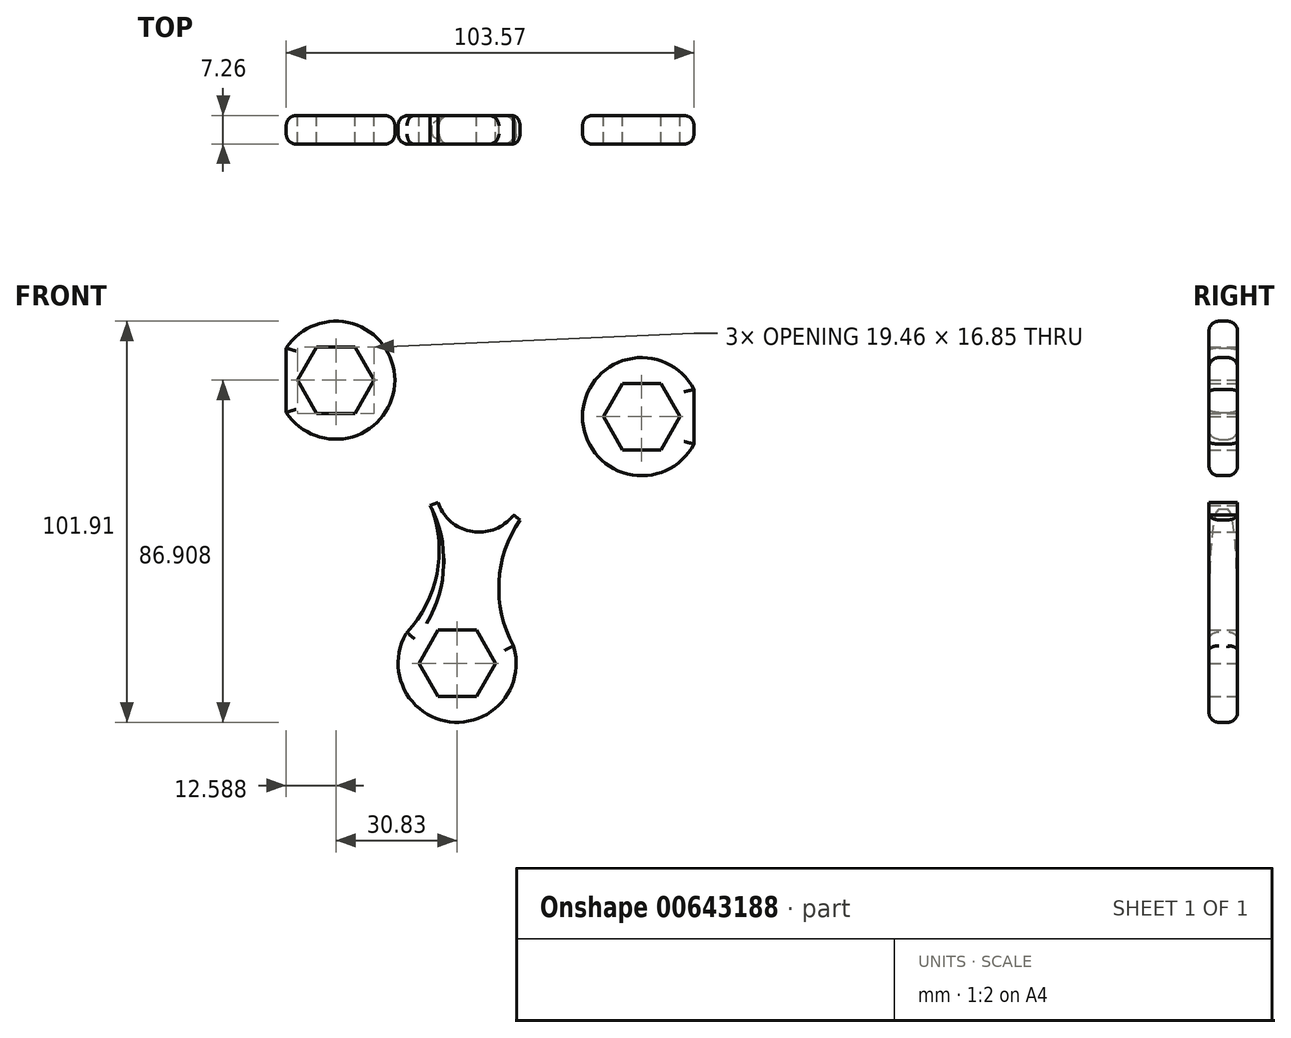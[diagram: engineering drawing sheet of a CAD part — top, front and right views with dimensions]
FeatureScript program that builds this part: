
annotation { "Feature Type Name" : "Feature", "Feature Type Description" : "" }
export const myFeature = defineFeature(function(context is Context, id is Id, definition is map)
    precondition{}
    {
        {
            var Q0;
            Q0=qCreatedBy(makeId("Front.planeOp"),FACE);
            var sketch = newSketch(context, id + "F0", { "sketchPlane" : qUnion([Q0])});
            skCircle(sketch, "E0.cCircle", {"center": v(-36.4, 27.6) * mm, "radius": 8.42 * mm, "construction": true});
            skLineSegment(sketch, "E0.0", {"start": v(-31.54, 19.17) * mm, "end": v(-41.27, 19.17) * mm});
            skLineSegment(sketch, "E0.1", {"start": v(-41.27, 19.17) * mm, "end": v(-46.13, 27.6) * mm});
            skLineSegment(sketch, "E0.2", {"start": v(-46.13, 27.6) * mm, "end": v(-41.27, 36.02) * mm});
            skLineSegment(sketch, "E0.3", {"start": v(-41.27, 36.02) * mm, "end": v(-31.54, 36.02) * mm});
            skLineSegment(sketch, "E0.4", {"start": v(-31.54, 36.02) * mm, "end": v(-26.67, 27.6) * mm});
            skLineSegment(sketch, "E0.5", {"start": v(-26.67, 27.6) * mm, "end": v(-31.54, 19.17) * mm});
            skPoint(sketch, "E0.0.midPoint", {"position": v(-36.4, 19.17) * mm});
            skCircle(sketch, "E1", {"center": v(-36.4, 27.6) * mm, "radius": 15 * mm});
            skCircle(sketch, "E2", {"center": v(0, 0) * mm, "radius": 11 * mm});
            skPoint(sketch, "E3.0.internal.snap0", {"position": v(-43.7, 31.81) * mm});
            skLineSegment(sketch, "E4", {"start": v(0, 0) * mm, "end": v(-36.4, 27.6) * mm});
            skPoint(sketch, "E5.1.0", {"position": v(1.72, -40.1) * mm});
            skCircle(sketch, "E5.1.1", {"center": v(-5.57, -44.3) * mm, "radius": 15 * mm});
            skCircle(sketch, "E5.1.2", {"center": v(-5.57, -44.3) * mm, "radius": 8.42 * mm, "construction": true});
            skLineSegment(sketch, "E5.1.3", {"start": v(-10.44, -35.88) * mm, "end": v(-0.7, -35.88) * mm});
            skLineSegment(sketch, "E5.1.4", {"start": v(0.13, 1.02) * mm, "end": v(-5.57, -44.3) * mm});
            skPoint(sketch, "E5.1.5", {"position": v(-5.57, -52.73) * mm});
            skLineSegment(sketch, "E5.1.6", {"start": v(-10.44, -52.73) * mm, "end": v(-15.3, -44.3) * mm});
            skLineSegment(sketch, "E5.1.7", {"start": v(4.16, -44.3) * mm, "end": v(-0.7, -52.73) * mm});
            skLineSegment(sketch, "E5.1.8", {"start": v(-0.7, -35.88) * mm, "end": v(4.16, -44.3) * mm});
            skLineSegment(sketch, "E5.1.9", {"start": v(-0.7, -52.73) * mm, "end": v(-10.44, -52.73) * mm});
            skLineSegment(sketch, "E5.1.10", {"start": v(-15.3, -44.3) * mm, "end": v(-10.44, -35.88) * mm});
            skPoint(sketch, "E5.2.0", {"position": v(33.99, 22.56) * mm});
            skCircle(sketch, "E5.2.1", {"center": v(41.29, 18.35) * mm, "radius": 15 * mm});
            skCircle(sketch, "E5.2.2", {"center": v(41.29, 18.35) * mm, "radius": 8.42 * mm, "construction": true});
            skLineSegment(sketch, "E5.2.3", {"start": v(36.42, 9.92) * mm, "end": v(31.56, 18.35) * mm});
            skLineSegment(sketch, "E5.2.4", {"start": v(-0.82, 0.62) * mm, "end": v(41.29, 18.35) * mm});
            skPoint(sketch, "E5.2.5", {"position": v(48.58, 22.56) * mm});
            skLineSegment(sketch, "E5.2.6", {"start": v(51.01, 18.35) * mm, "end": v(46.15, 9.92) * mm});
            skLineSegment(sketch, "E5.2.7", {"start": v(36.42, 26.77) * mm, "end": v(46.15, 26.77) * mm});
            skLineSegment(sketch, "E5.2.8", {"start": v(31.56, 18.35) * mm, "end": v(36.42, 26.77) * mm});
            skLineSegment(sketch, "E5.2.9", {"start": v(46.15, 26.77) * mm, "end": v(51.01, 18.35) * mm});
            skLineSegment(sketch, "E5.2.10", {"start": v(46.15, 9.92) * mm, "end": v(36.42, 9.92) * mm});
            skPoint(sketch, "E5.center", {"position": v(-0.23, 0.55) * mm});
            skLineSegment(sketch, "E6", {"start": v(-36.4, 27.6) * mm, "end": v(50.1, -37.98) * mm});
            skLineSegment(sketch, "E7", {"start": v(41.29, 18.35) * mm, "end": v(-48.92, -19.63) * mm});
            skArc(sketch, "E8", {"start": v(10.38, -7.87) * mm, "mid": v(5.04, -23.76) * mm, "end": v(8.82, -40.1) * mm});
            skArc(sketch, "E9.MirrorCS", {"start": v(-12, -5.05) * mm, "mid": v(-10.77, -21.77) * mm, "end": v(-18.48, -36.66) * mm});
            skArc(sketch, "E10.1.0", {"start": v(10.38, -7.87) * mm, "mid": v(24.24, 1.56) * mm, "end": v(40.99, 2.33) * mm});
            skArc(sketch, "E10.1.1", {"start": v(1.62, 12.92) * mm, "mid": v(18.06, 16.25) * mm, "end": v(30.31, 27.69) * mm});
            skArc(sketch, "E10.2.0", {"start": v(1.62, 12.92) * mm, "mid": v(-13.47, 20.21) * mm, "end": v(-22.51, 34.33) * mm});
            skArc(sketch, "E10.2.1", {"start": v(-12, -5.05) * mm, "mid": v(-23.1, 7.51) * mm, "end": v(-39.14, 12.4) * mm});
            skLineSegment(sketch, "E11", {"start": v(-48.99, 55.53) * mm, "end": v(-48.99, -54.39) * mm});
            skLineSegment(sketch, "E12", {"start": v(54.58, 55.9) * mm, "end": v(54.58, -54.2) * mm});
            skSolve(sketch);
        }
        {
            var Q0;
            {var subQ1=sQuery(id+"F0.wireOp",EDGE,"E1");var subQ11=sQuery(id+"F0.wireOp",EDGE,"E10.2.0");var subQ12=makeQuery(id+"F0.imprint","INTERSECT",VERTEX,{"disambiguationData":[OD(1.0)],"derivedFrom":[subQ1,subQ11]});Q0=makeQuery(id+"F0.imprint","IMPRINT",FACE,{"disambiguationData":[TD([[makeQuery(id+"F0.imprint","IMPRINT",EDGE,{"disambiguationData":[TD([[subQ12,1.0]])],"derivedFrom":subQ1}),-1.0]])]});}
            var Q1;
            {var subQ0=sQuery(id+"F0.wireOp",EDGE,"E7");var subQ3=sQuery(id+"F0.wireOp",EDGE,"E2");var subQ4=makeQuery(id+"F0.imprint","INTERSECT",VERTEX,{"disambiguationData":[OD(0.0)],"derivedFrom":[subQ3,subQ0]});Q1=makeQuery(id+"F0.imprint","IMPRINT",FACE,{"disambiguationData":[TD([[makeQuery(id+"F0.imprint","IMPRINT",EDGE,{"disambiguationData":[TD([[subQ4,1.0]])],"derivedFrom":subQ3}),-1.0]])]});}
            var Q2;
            {var subQ3=sQuery(id+"F0.wireOp",EDGE,"E2");var subQ5=sQuery(id+"F0.wireOp",EDGE,"E5.1.4");var subQ6=makeQuery(id+"F0.imprint","INTERSECT",VERTEX,{"derivedFrom":[subQ3,subQ5]});Q2=makeQuery(id+"F0.imprint","IMPRINT",FACE,{"disambiguationData":[TD([[makeQuery(id+"F0.imprint","IMPRINT",EDGE,{"disambiguationData":[TD([[subQ6,-1.0]])],"derivedFrom":subQ3}),-1.0]])]});}
            var Q3;
            {var subQ1=sQuery(id+"F0.wireOp",EDGE,"E7");var subQ3=sQuery(id+"F0.wireOp",EDGE,"E2");var subQ4=makeQuery(id+"F0.imprint","INTERSECT",VERTEX,{"disambiguationData":[OD(1.0)],"derivedFrom":[subQ3,subQ1]});Q3=makeQuery(id+"F0.imprint","IMPRINT",FACE,{"disambiguationData":[TD([[makeQuery(id+"F0.imprint","IMPRINT",EDGE,{"disambiguationData":[TD([[subQ4,-1.0]])],"derivedFrom":subQ3}),-1.0]])]});}
            var Q4;
            {var subQ0=sQuery(id+"F0.wireOp",EDGE,"E10.2.1");var subQ5=sQuery(id+"F0.wireOp",EDGE,"E1");var subQ6=makeQuery(id+"F0.imprint","INTERSECT",VERTEX,{"disambiguationData":[OD(1.0)],"derivedFrom":[subQ5,subQ0]});Q4=makeQuery(id+"F0.imprint","IMPRINT",FACE,{"disambiguationData":[TD([[makeQuery(id+"F0.imprint","IMPRINT",EDGE,{"disambiguationData":[TD([[subQ6,-1.0]])],"derivedFrom":subQ5}),-1.0]])]});}
            extrude(context, id + "F1", {"entities" : qUnion([Q0, Q1, Q2, Q3, Q4]), "endBound" : BoundingType.SYMMETRIC, "depth" : 7.25 * mm, "offsetDistance" : 25 * mm});
        }
        {
            var Q0;
            {var subQ9=sQuery(id+"F0.wireOp",EDGE,"E0.0");Q0=makeQuery(id+"F0.imprint","IMPRINT",FACE,{"disambiguationData":[TD([[makeQuery(id+"F0.imprint","IMPRINT",EDGE,{"derivedFrom":subQ9}),1.0]])]});}
            var Q1;
            Q1=makeQuery(id+"F0.imprint","IMPRINT",FACE,{"disambiguationData":[TD([[makeQuery(id+"F0.imprint","IMPRINT",EDGE,{"derivedFrom":sQuery(id+"F0.wireOp",EDGE,"E5.2.6")}),1.0]])]});
            var Q2;
            Q2=makeQuery(id+"F0.imprint","IMPRINT",FACE,{"disambiguationData":[TD([[makeQuery(id+"F0.imprint","IMPRINT",EDGE,{"derivedFrom":sQuery(id+"F0.wireOp",EDGE,"E5.1.6")}),1.0]])]});
            extrude(context, id + "F2", {"entities" : qUnion([Q0, Q1, Q2]), "operationType" : NewBodyOperationType.ADD, "endBound" : BoundingType.SYMMETRIC, "depth" : 7.25 * mm, "offsetDistance" : 25 * mm});
        }
        {
            var Q0;
            {var subQ0=sQuery(id+"F0.wireOp",EDGE,"E9.MirrorCS");Q0=makeQuery(id+"F2.boolean.opBoolean","MERGE",EDGE,{"derivedFrom":[makeQuery(id+"F1.opExtrude","CAP_EDGE",EDGE,{"disambiguationData":[OSD([subQ0])],"isStart":true}),makeQuery(id+"F2.opExtrude","CAP_EDGE",EDGE,{"disambiguationData":[OSD([subQ0])],"isStart":true})]});}
            var Q1;
            {var subQ0=sQuery(id+"F0.wireOp",EDGE,"E10.2.1");Q1=makeQuery(id+"F2.boolean.opBoolean","MERGE",EDGE,{"derivedFrom":[makeQuery(id+"F1.opExtrude","CAP_EDGE",EDGE,{"disambiguationData":[OSD([subQ0])],"isStart":true}),makeQuery(id+"F2.opExtrude","CAP_EDGE",EDGE,{"disambiguationData":[OSD([subQ0])],"isStart":true})]});}
            var Q2;
            {var subQ0=sQuery(id+"F0.wireOp",EDGE,"E9.MirrorCS");Q2=makeQuery(id+"F2.boolean.opBoolean","MERGE",EDGE,{"derivedFrom":[makeQuery(id+"F1.opExtrude","CAP_EDGE",EDGE,{"disambiguationData":[OSD([subQ0])],"isStart":false}),makeQuery(id+"F2.opExtrude","CAP_EDGE",EDGE,{"disambiguationData":[OSD([subQ0])],"isStart":false})]});}
            var Q3;
            {var subQ0=sQuery(id+"F0.wireOp",EDGE,"E10.2.1");Q3=makeQuery(id+"F2.boolean.opBoolean","MERGE",EDGE,{"derivedFrom":[makeQuery(id+"F1.opExtrude","CAP_EDGE",EDGE,{"disambiguationData":[OSD([subQ0])],"isStart":false}),makeQuery(id+"F2.opExtrude","CAP_EDGE",EDGE,{"disambiguationData":[OSD([subQ0])],"isStart":false})]});}
            var Q4;
            {var subQ0=sQuery(id+"F0.wireOp",EDGE,"E10.2.0");Q4=makeQuery(id+"F2.boolean.opBoolean","MERGE",EDGE,{"derivedFrom":[makeQuery(id+"F1.opExtrude","CAP_EDGE",EDGE,{"disambiguationData":[OSD([subQ0])],"isStart":true}),makeQuery(id+"F2.opExtrude","CAP_EDGE",EDGE,{"disambiguationData":[OSD([subQ0])],"isStart":true})]});}
            var Q5;
            {var subQ0=sQuery(id+"F0.wireOp",EDGE,"E10.2.0");Q5=makeQuery(id+"F2.boolean.opBoolean","MERGE",EDGE,{"derivedFrom":[makeQuery(id+"F1.opExtrude","CAP_EDGE",EDGE,{"disambiguationData":[OSD([subQ0])],"isStart":false}),makeQuery(id+"F2.opExtrude","CAP_EDGE",EDGE,{"disambiguationData":[OSD([subQ0])],"isStart":false})]});}
            var Q6;
            {var subQ0=sQuery(id+"F0.wireOp",EDGE,"E10.1.1");Q6=makeQuery(id+"F2.boolean.opBoolean","MERGE",EDGE,{"derivedFrom":[makeQuery(id+"F1.opExtrude","CAP_EDGE",EDGE,{"disambiguationData":[OSD([subQ0])],"isStart":false}),makeQuery(id+"F2.opExtrude","CAP_EDGE",EDGE,{"disambiguationData":[OSD([subQ0])],"isStart":false})]});}
            var Q7;
            {var subQ0=sQuery(id+"F0.wireOp",EDGE,"E10.1.1");Q7=makeQuery(id+"F2.boolean.opBoolean","MERGE",EDGE,{"derivedFrom":[makeQuery(id+"F1.opExtrude","CAP_EDGE",EDGE,{"disambiguationData":[OSD([subQ0])],"isStart":true}),makeQuery(id+"F2.opExtrude","CAP_EDGE",EDGE,{"disambiguationData":[OSD([subQ0])],"isStart":true})]});}
            var Q8;
            {var subQ0=sQuery(id+"F0.wireOp",EDGE,"E10.1.0");Q8=makeQuery(id+"F2.boolean.opBoolean","MERGE",EDGE,{"derivedFrom":[makeQuery(id+"F1.opExtrude","CAP_EDGE",EDGE,{"disambiguationData":[OSD([subQ0])],"isStart":true}),makeQuery(id+"F2.opExtrude","CAP_EDGE",EDGE,{"disambiguationData":[OSD([subQ0])],"isStart":true})]});}
            var Q9;
            {var subQ0=sQuery(id+"F0.wireOp",EDGE,"E10.1.0");Q9=makeQuery(id+"F2.boolean.opBoolean","MERGE",EDGE,{"derivedFrom":[makeQuery(id+"F1.opExtrude","CAP_EDGE",EDGE,{"disambiguationData":[OSD([subQ0])],"isStart":false}),makeQuery(id+"F2.opExtrude","CAP_EDGE",EDGE,{"disambiguationData":[OSD([subQ0])],"isStart":false})]});}
            var Q10;
            {var subQ0=sQuery(id+"F0.wireOp",EDGE,"E8");Q10=makeQuery(id+"F2.boolean.opBoolean","MERGE",EDGE,{"derivedFrom":[makeQuery(id+"F1.opExtrude","CAP_EDGE",EDGE,{"disambiguationData":[OSD([subQ0])],"isStart":false}),makeQuery(id+"F2.opExtrude","CAP_EDGE",EDGE,{"disambiguationData":[OSD([subQ0])],"isStart":false})]});}
            var Q11;
            {var subQ0=sQuery(id+"F0.wireOp",EDGE,"E8");Q11=makeQuery(id+"F2.boolean.opBoolean","MERGE",EDGE,{"derivedFrom":[makeQuery(id+"F1.opExtrude","CAP_EDGE",EDGE,{"disambiguationData":[OSD([subQ0])],"isStart":true}),makeQuery(id+"F2.opExtrude","CAP_EDGE",EDGE,{"disambiguationData":[OSD([subQ0])],"isStart":true})]});}
            fillet(context, id + "F3", {"entities" : qUnion([Q0, Q1, Q2, Q3, Q4, Q5, Q6, Q7, Q8, Q9, Q10, Q11]), "radius" : 2.5 * mm, "tangentPropagation" : true, "allowEdgeOverflow" : false});
        }
        {
            var Q0;
            {var subQ0=sQuery(id+"F0.wireOp",EDGE,"E5.2.1");Q0=makeQuery(id+"F2.opExtrude","CAP_EDGE",EDGE,{"disambiguationData":[OSD([subQ0]),TDD([makeQuery(id+"F0.imprint","IMPRINT",EDGE,{"disambiguationData":[TD([[makeQuery(id+"F0.imprint","INTERSECT",VERTEX,{"disambiguationData":[OD(0.0)],"derivedFrom":[subQ0,sQuery(id+"F0.wireOp",EDGE,"E10.1.0")]}),-1.0]])],"derivedFrom":subQ0})])],"isStart":true});}
            var Q1;
            {var subQ0=sQuery(id+"F0.wireOp",EDGE,"E5.2.1");Q1=makeQuery(id+"F2.opExtrude","CAP_EDGE",EDGE,{"disambiguationData":[OSD([subQ0]),TDD([makeQuery(id+"F0.imprint","IMPRINT",EDGE,{"disambiguationData":[TD([[makeQuery(id+"F0.imprint","INTERSECT",VERTEX,{"disambiguationData":[OD(0.0)],"derivedFrom":[subQ0,sQuery(id+"F0.wireOp",EDGE,"E10.1.1")]}),1.0]])],"derivedFrom":subQ0})])],"isStart":true});}
            var Q2;
            {var subQ0=sQuery(id+"F0.wireOp",EDGE,"E5.2.1");Q2=makeQuery(id+"F2.opExtrude","CAP_EDGE",EDGE,{"disambiguationData":[OSD([subQ0]),TDD([makeQuery(id+"F0.imprint","IMPRINT",EDGE,{"disambiguationData":[TD([[makeQuery(id+"F0.imprint","INTERSECT",VERTEX,{"disambiguationData":[OD(0.0)],"derivedFrom":[subQ0,sQuery(id+"F0.wireOp",EDGE,"E10.1.1")]}),1.0]])],"derivedFrom":subQ0})])],"isStart":false});}
            var Q3;
            {var subQ0=sQuery(id+"F0.wireOp",EDGE,"E5.1.1");Q3=makeQuery(id+"F2.opExtrude","CAP_EDGE",EDGE,{"disambiguationData":[OSD([subQ0]),TDD([makeQuery(id+"F0.imprint","IMPRINT",EDGE,{"disambiguationData":[TD([[makeQuery(id+"F0.imprint","INTERSECT",VERTEX,{"disambiguationData":[OD(0.0)],"derivedFrom":[subQ0,sQuery(id+"F0.wireOp",EDGE,"E8")]}),1.0]])],"derivedFrom":subQ0})])],"isStart":true});}
            var Q4;
            {var subQ0=sQuery(id+"F0.wireOp",EDGE,"E5.1.1");Q4=makeQuery(id+"F2.opExtrude","CAP_EDGE",EDGE,{"disambiguationData":[OSD([subQ0]),TDD([makeQuery(id+"F0.imprint","IMPRINT",EDGE,{"disambiguationData":[TD([[makeQuery(id+"F0.imprint","INTERSECT",VERTEX,{"disambiguationData":[OD(0.0)],"derivedFrom":[subQ0,sQuery(id+"F0.wireOp",EDGE,"E8")]}),1.0]])],"derivedFrom":subQ0})])],"isStart":false});}
            var Q5;
            {var subQ0=sQuery(id+"F0.wireOp",EDGE,"E1");Q5=makeQuery(id+"F2.opExtrude","CAP_EDGE",EDGE,{"disambiguationData":[OSD([subQ0]),TDD([makeQuery(id+"F0.imprint","IMPRINT",EDGE,{"disambiguationData":[TD([[makeQuery(id+"F0.imprint","INTERSECT",VERTEX,{"disambiguationData":[OD(0.0)],"derivedFrom":[subQ0,sQuery(id+"F0.wireOp",EDGE,"E10.2.0")]}),-1.0]])],"derivedFrom":subQ0})])],"isStart":true});}
            var Q6;
            {var subQ0=sQuery(id+"F0.wireOp",EDGE,"E1");Q6=makeQuery(id+"F2.opExtrude","CAP_EDGE",EDGE,{"disambiguationData":[OSD([subQ0]),TDD([makeQuery(id+"F0.imprint","IMPRINT",EDGE,{"disambiguationData":[TD([[makeQuery(id+"F0.imprint","INTERSECT",VERTEX,{"disambiguationData":[OD(0.0)],"derivedFrom":[subQ0,sQuery(id+"F0.wireOp",EDGE,"E10.2.1")]}),1.0]])],"derivedFrom":subQ0})])],"isStart":true});}
            var Q7;
            Q7=makeQuery(id+"F2.opExtrude","CAP_EDGE",EDGE,{"disambiguationData":[OSD([sQuery(id+"F0.wireOp",EDGE,"E11")])],"isStart":true});
            var Q8;
            {var subQ0=sQuery(id+"F0.wireOp",EDGE,"E1");Q8=makeQuery(id+"F2.opExtrude","CAP_EDGE",EDGE,{"disambiguationData":[OSD([subQ0]),TDD([makeQuery(id+"F0.imprint","IMPRINT",EDGE,{"disambiguationData":[TD([[makeQuery(id+"F0.imprint","INTERSECT",VERTEX,{"disambiguationData":[OD(0.0)],"derivedFrom":[subQ0,sQuery(id+"F0.wireOp",EDGE,"E10.2.0")]}),-1.0]])],"derivedFrom":subQ0})])],"isStart":false});}
            var Q9;
            {var subQ0=sQuery(id+"F0.wireOp",EDGE,"E1");Q9=makeQuery(id+"F2.opExtrude","CAP_EDGE",EDGE,{"disambiguationData":[OSD([subQ0]),TDD([makeQuery(id+"F0.imprint","IMPRINT",EDGE,{"disambiguationData":[TD([[makeQuery(id+"F0.imprint","INTERSECT",VERTEX,{"disambiguationData":[OD(0.0)],"derivedFrom":[subQ0,sQuery(id+"F0.wireOp",EDGE,"E10.2.1")]}),1.0]])],"derivedFrom":subQ0})])],"isStart":false});}
            var Q10;
            Q10=makeQuery(id+"F2.opExtrude","CAP_EDGE",EDGE,{"disambiguationData":[OSD([sQuery(id+"F0.wireOp",EDGE,"E11")])],"isStart":false});
            var Q11;
            Q11=makeQuery(id+"F2.opExtrude","CAP_EDGE",EDGE,{"disambiguationData":[OSD([sQuery(id+"F0.wireOp",EDGE,"E12")])],"isStart":false});
            var Q12;
            Q12=makeQuery(id+"F2.opExtrude","CAP_EDGE",EDGE,{"disambiguationData":[OSD([sQuery(id+"F0.wireOp",EDGE,"E12")])],"isStart":true});
            fillet(context, id + "F4", {"entities" : qUnion([Q0, Q1, Q2, Q3, Q4, Q5, Q6, Q7, Q8, Q9, Q10, Q11, Q12]), "radius" : 2.5 * mm, "tangentPropagation" : true, "allowEdgeOverflow" : false});
        }
    });
